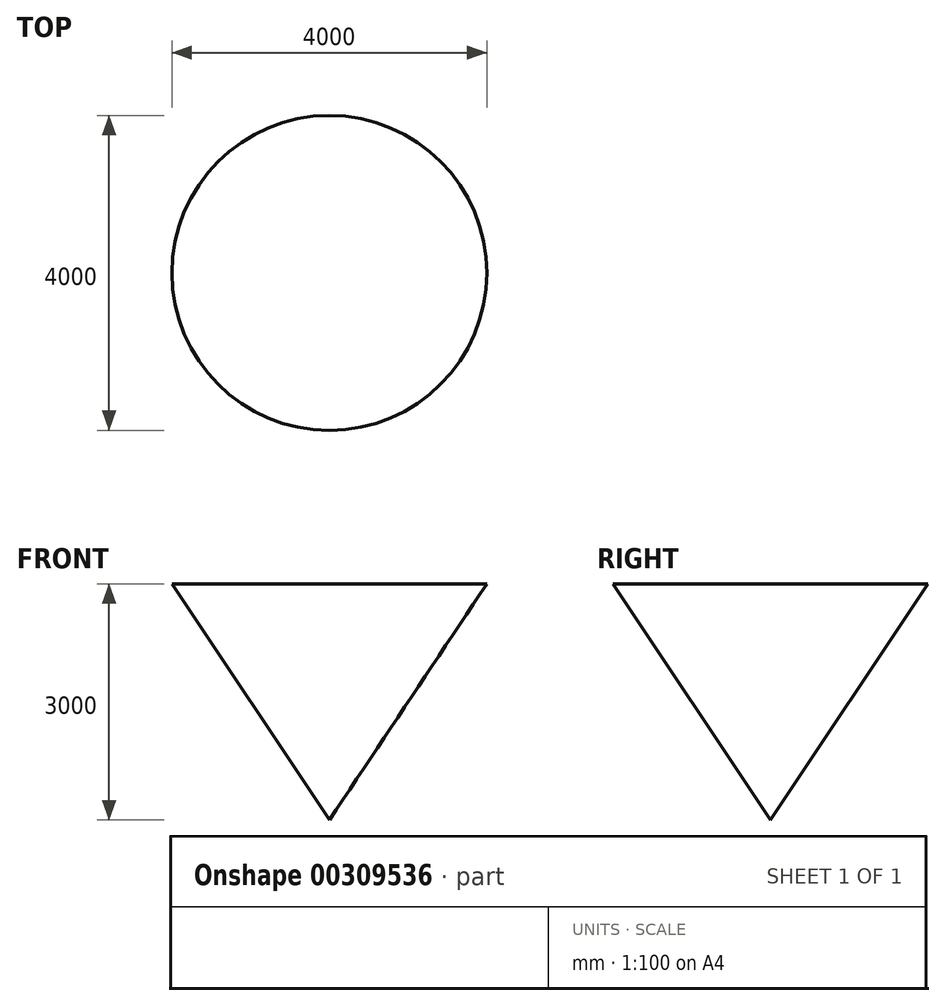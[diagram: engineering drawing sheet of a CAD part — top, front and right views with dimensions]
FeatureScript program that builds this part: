
annotation { "Feature Type Name" : "Feature", "Feature Type Description" : "" }
export const myFeature = defineFeature(function(context is Context, id is Id, definition is map)
    precondition{}
    {
        {
            var Q0;
            Q0=qCreatedBy(makeId("Front.planeOp"),FACE);
            var sketch = newSketch(context, id + "F0", { "sketchPlane" : qUnion([Q0])});
            skLineSegment(sketch, "E0", {"start": v(0, 0) * mm, "end": v(0, -3000) * mm});
            skLineSegment(sketch, "E1", {"start": v(0, -3000) * mm, "end": v(2000, 0) * mm});
            skLineSegment(sketch, "E2", {"start": v(2000, 0) * mm, "end": v(0, 0) * mm});
            skSolve(sketch);
        }
        {
            var Q0;
            Q0 = qSketchRegion(id + "F0", true);
            var Q1;
            Q1=sQuery(id+"F0.wireOp",EDGE,"E0");
            revolve(context, id + "F1", {"entities" : qUnion([Q0]), "axis" : qUnion([Q1]), "revolveType" : RevolveType.FULL});
        }
    });
